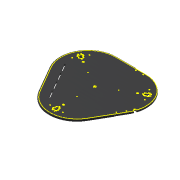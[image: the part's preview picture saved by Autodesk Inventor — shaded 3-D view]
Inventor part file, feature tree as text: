
AUTODESK INVENTOR PART (.ipt)
format: ipt  version: 2016 (Build 200138000, 138)  size: 650,752 bytes
history: native  units: mm
features: sketch x15, extrude x13, thread x4, hole x4, fillet x2, pattern_circular x2, reference x2, projected_geometry x2
ambient origin geometry x8: Origin, YZ Plane, XZ Plane, XY Plane, X Axis, Y Axis, Z Axis, Center Point
bodies: Solid1 (feature_tree)
feature tree (44):
  extrude  "Extrusion1"  Depth=8.0mm
  extrude  "Extrusion2"  Depth=2.5mm
  extrude  "Extrusion3"  Depth=6.4mm
  fillet  "Fillet1"  Radius=20.0mm
  extrude  "Extrusion4"  Depth=18.0mm
  pattern_circular  "Circular Pattern1"  [2 undecoded]
  extrude  "Extrusion6"  Depth=10.0mm TaperAngle=0.0deg
  extrude  "Extrusion7"  Depth=4.0mm
  extrude  "Extrusion8"  Depth=6.5mm
  extrude  "Extrusion9"  Depth=4.0mm TaperAngle=0.0deg
  thread  "Thread1"  [1 undecoded]
  thread  "Thread2"  [1 undecoded]
  thread  "Thread3"  [1 undecoded]
  thread  "Thread4"  [1 undecoded]
  extrude  "Extrusion11"  Depth=4.0mm
  extrude  "Extrusion12"  Depth=8.0mm
  hole  "Hole1"  [1 undecoded]
  hole  "Hole2"  [1 undecoded]
  hole  "Hole3"  [1 undecoded]
  extrude  "Extrusion14"  Depth=3.2mm
  sketch  "Sketch15"  dims[d18=1.5mm]
  hole  "Hole4"  [1 undecoded]
  pattern_circular  "Circular Pattern2"  [2 undecoded]
  extrude  "Extrusion15"  Depth=1.5mm
  fillet  "Fillet2"  Radius=6.0mm
  extrude  "Extrusion16"  Depth=6.0mm
  sketch  "Sketch1"  dims[d0=8.0mm d1=0.0mm d2=24.0mm]
  reference  "Reference1"
  sketch  "Sketch2"  dims[d3=24.0mm d4=2.5mm]
  projected_geometry  "Projected Loop1"
  sketch  "Sketch3"  dims[d5=7.0mm d6=3.7mm d7=6.4mm d8=20.0mm]
  sketch  "Sketch4"  dims[d9=18.0mm d10=18.0mm]
  sketch  "Sketch6"  dims[d11=3.7mm]
  sketch  "Sketch7"  dims[d12=6.4mm]
  sketch  "Sketch8"  dims[d13=0.7mm]
  projected_geometry  "Projected Loop2"
  sketch  "Sketch9"  dims[d14=0.7mm]
  sketch  "Sketch11"  dims[d15=14.0mm]
  sketch  "Sketch12"  dims[d16=21.0mm]
  sketch  "Sketch14"  dims[d17=3.0mm]
  reference  "Reference2"
  sketch  "Sketch16"  dims[d19=1.5mm]
  sketch  "Sketch17"  dims[d20=1.5mm]
  sketch  "Sketch18"  dims[d21=3.0mm d22=3.0mm d23=10.0mm d24=0.0mm d25=4.0mm d26=6.5mm d28=4.0mm d29=0.0mm d30=2.0mm d31=12.0mm d32=2.5mm d33=2.5mm d34=4.0mm d35=15.0mm d36=15.0mm d37=2.4mm d38=0.0mm d39=30.0mm d40=360.0deg d45=3.2mm d46=1.0mm d47=0.0mm d48=3.0mm d49=0.0mm d50=1.5mm d51=6.0mm d52=6.0mm d53=10.0mm d54=0.0mm d55=3.2mm d56=23.0mm d57=3.2mm d58=23.0mm d59=1.7mm d60=0.0mm d61=0.0mm d62=3.25mm d63=3.25mm d64=5.8mm d65=5.8mm d66=6.0mm d67=6.0mm d68=15.0mm d69=0.0mm d70=3.25mm d71=3.25mm d72=5.8mm d73=5.8mm d74=6.0mm d75=32.5mm d76=10.0mm d77=0.0mm d78=10.0mm d79=0.0mm d80=10.0mm d81=0.0mm d82=10.0mm d83=0.0mm d87=10.0mm d88=20.0mm d89=20.0mm d90=0.0mm d91=240.0mm d92=7.5mm d93=7.5mm d94=7.5mm d95=2.0mm d96=0.0mm d97=10.0mm d98=10.0mm d99=3.0mm d100=6.0mm d101=4.0mm d102=2.0mm d103=90.0deg d104=8.0mm d105=20.594885mm d106=10.0mm d107=10.0mm d108=3.0mm d109=6.0mm d110=4.0mm d111=2.0mm d112=90.0deg d113=8.0mm d114=20.594885mm d115=10.0mm d116=10.0mm d117=3.0mm d118=6.0mm d119=4.0mm d120=2.0mm d121=90.0deg d122=8.0mm d123=20.594885mm d144=10.0mm d145=0.0mm d146=3.0mm d147=5.0mm d148=2.459mm d149=4.0mm d150=4.0mm d151=2.0mm d152=90.0deg d153=7.0mm d154=20.594885mm d155=30.0mm d156=360.0deg d162=6.0mm d163=190.0mm d164=9.5mm d165=9.0mm d166=9.5mm d167=40.5mm d168=40.5mm d169=40.5mm d170=35.0mm d171=10.0mm d172=0.0mm d173=2.0mm d174=8.0mm d175=0.0mm]
note: 12 required parameter values undecoded (feature->parameter linkage not recoverable at this tier; creation-order binding heuristic only, values carry confidence <= 0.55)
